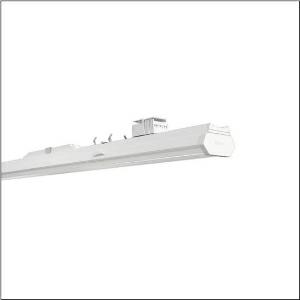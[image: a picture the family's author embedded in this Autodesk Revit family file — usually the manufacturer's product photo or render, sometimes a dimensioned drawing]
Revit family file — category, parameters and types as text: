
# Revit family: licross_r__11_protected_ho_51tp13dn4exrd_cf40
name_source: partatom
category: Lighting Fixtures
units: mm (PartAtom-declared; Revit-internal decimal feet)

## family parameters
Cut with Voids When Loaded = No
Host = Face
Light Source = No
Part Type = Normal
Room Calculation Point = No
Round Connector Dimension = Use Diameter
Shared = No

## types (1)
- --- (1 x LED, 2220 lm, 14.3 W, 4000K)
    Apparent Load = 14 VA
    CIE Flux Codes = 89 96 99 100 99
    Color Rendering = 80
    Color Temperature = 4000K
    Default Elevation = 1800 mm
    Description = Licross® 11 Protected HOluminaire insert, length: 1.500mm, width: 90mm, height: 101mm, LED rated luminous flux: 14.170lm, light colour: 840, control gear: DALI 2, control gear: ECG DALI, with plug, 6-pole, with phase selection, mains connection: 220..240V, AC/DC, 0/50..60Hz, without changeover relay, for emergency light function, for central battery installations according to DIN EN 60598-2-22, halogen-free wiring, primary optical cover: cover, of PMMA, light emission: direct distribution, protection rating (complete): IP64, insulation class (complete): insulation class I (protective earthing), certification: CE, ENEC, VDE, protection symbol: D if used in an environment without relevant dust loads with corresponding accessories, permissible ambient temperature for indoor applications: -25..+35°C, standard: EN 60598-2-22, reducing of maximum allowable ambient temperature of 5°C with ceiling mounting, corresponds to IFS (International Featured Standards) requirements for safety and quality in the food industry, packaging unit: 1 piece
    Height = 92 mm
    Lamp = 1 x LED
    Lamp Light Flux = 2220 lm
    Lamp Power = 14.3 W
    Lamp count = 1
    Length = 1500 mm
    Luminous efficacy = 155 lm/W
    Manufacturer = Siteco
    ModVariant = No
    Model = 51TP13DN4EXRD
    Mounting Place = Ceiling
    Mounting Type = Pendant
    Number of Poles = 1
    OnlyDefault = Yes
    Power Factor = 1
    Product Name = Licross® 11 Protected HO
    Product group = luminaire insert
    ProductGroupID = 902
    Protection Class = Protection class I
    Protection Degree = IP 64
    RLX_Detail_Level = 1
    RlxData = <blob elided: 24337 chars, md5=6c141e4a>
    Socket = socket
    Standby Power = 0 W
    System Light Flux = 2220 lm
    System Power = 14 W
    Type Comments = : DC mode (central or group accumulator) initial emergency light level
    Type Image = l_1256148.jpg
    URL = http://relux.com
    VarID = @adj_134529
    Voltage = 0 V
    Weight = 0.00 kg
    Width = 88 mm

## geometry (parser evidence)
native form markers: Blend x4, Sweep x11
no freeform markers — native parametric forms only
